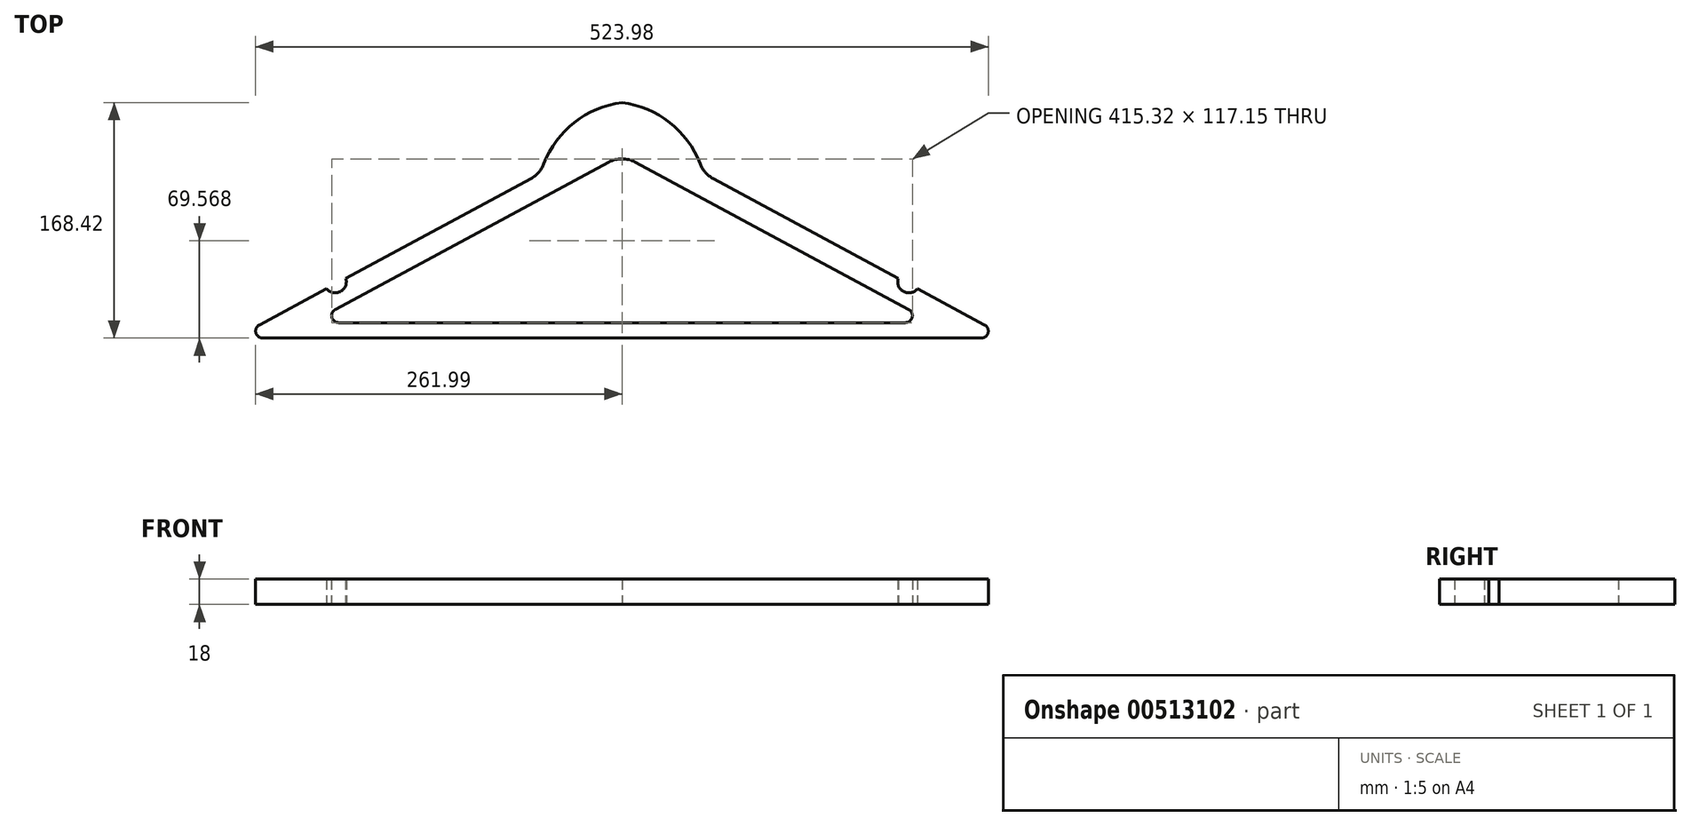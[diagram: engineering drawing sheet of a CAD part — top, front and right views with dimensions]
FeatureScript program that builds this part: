
annotation { "Feature Type Name" : "Feature", "Feature Type Description" : "" }
export const myFeature = defineFeature(function(context is Context, id is Id, definition is map)
    precondition{}
    {
        {
            var Q0;
            Q0=qCreatedBy(makeId("Top.planeOp"),FACE);
            var sketch = newSketch(context, id + "F0", { "sketchPlane" : qUnion([Q0])});
            skLineSegment(sketch, "E0", {"start": v(-230.49, 94.94) * mm, "end": v(174.87, 94.94) * mm});
            skLineSegment(sketch, "E1", {"start": v(-232.86, 104.34) * mm, "end": v(-37.3, 209.7) * mm});
            skLineSegment(sketch, "E2", {"start": v(-18.32, 209.7) * mm, "end": v(177.24, 104.34) * mm});
            skLineSegment(sketch, "E3", {"start": v(-287.17, 93.36) * mm, "end": v(-239.12, 119.24) * mm});
            skLineSegment(sketch, "E4", {"start": v(37.3, 198) * mm, "end": v(169.75, 126.65) * mm});
            skLineSegment(sketch, "E5", {"start": v(229.18, 83.95) * mm, "end": v(-284.8, 83.95) * mm});
            skLineSegment(sketch, "E6", {"start": v(-27.81, 214.81) * mm, "end": v(-27.81, -26.53) * mm, "construction": true});
            skLineSegment(sketch, "E7", {"start": v(-27.81, -26.53) * mm, "end": v(-27.81, 281.21) * mm, "construction": true});
            skPoint(sketch, "E8.visualSharp", {"position": v(-304.62, 83.95) * mm});
            skArc(sketch, "E8.filletArc", {"start": v(-287.17, 93.36) * mm, "mid": v(-289.64, 87.73) * mm, "end": v(-284.8, 83.95) * mm});
            skPoint(sketch, "E9.visualSharp", {"position": v(249, 83.95) * mm});
            skArc(sketch, "E9.filletArc", {"start": v(229.18, 83.95) * mm, "mid": v(234.02, 87.73) * mm, "end": v(231.55, 93.36) * mm});
            skPoint(sketch, "E10.visualSharp", {"position": v(-250.31, 94.94) * mm});
            skArc(sketch, "E10.filletArc", {"start": v(-232.86, 104.34) * mm, "mid": v(-235.34, 98.72) * mm, "end": v(-230.49, 94.94) * mm});
            skPoint(sketch, "E11.visualSharp", {"position": v(194.69, 94.94) * mm});
            skArc(sketch, "E11.filletArc", {"start": v(174.87, 94.94) * mm, "mid": v(179.71, 98.72) * mm, "end": v(177.24, 104.34) * mm});
            skPoint(sketch, "E12.visualSharp", {"position": v(-27.81, 256.12) * mm});
            skPoint(sketch, "E13.visualSharp", {"position": v(-27.81, 214.81) * mm});
            skArc(sketch, "E13.filletArc", {"start": v(-18.32, 209.7) * mm, "mid": v(-27.81, 212.1) * mm, "end": v(-37.3, 209.7) * mm});
            skArc(sketch, "E14", {"start": v(-27.78, 252.37) * mm, "mid": v(-61.8, 238.06) * mm, "end": v(-83.76, 208.4) * mm});
            skArc(sketch, "E15.MirrorCS", {"start": v(-27.85, 252.37) * mm, "mid": v(6.18, 238.06) * mm, "end": v(28.14, 208.4) * mm});
            skPoint(sketch, "E16.visualSharp", {"position": v(-85.95, 201.76) * mm});
            skArc(sketch, "E16.filletArc", {"start": v(-92.92, 198) * mm, "mid": v(-87.41, 202.38) * mm, "end": v(-83.76, 208.4) * mm});
            skPoint(sketch, "E17.visualSharp", {"position": v(30.33, 201.76) * mm});
            skArc(sketch, "E17.filletArc", {"start": v(28.14, 208.4) * mm, "mid": v(31.8, 202.38) * mm, "end": v(37.3, 198) * mm});
            skArc(sketch, "E18", {"start": v(-239.12, 119.24) * mm, "mid": v(-229.14, 117.17) * mm, "end": v(-225.37, 126.65) * mm});
            skLineSegment(sketch, "E19.trimOffspring", {"start": v(-225.37, 126.65) * mm, "end": v(-92.92, 198) * mm});
            skArc(sketch, "E20.MirrorCS", {"start": v(183.5, 119.24) * mm, "mid": v(173.51, 117.17) * mm, "end": v(169.75, 126.65) * mm});
            skLineSegment(sketch, "E21.trimOffspring", {"start": v(183.5, 119.24) * mm, "end": v(231.55, 93.36) * mm});
            skSolve(sketch);
        }
        {
            var Q0;
            Q0=makeQuery(id+"F0.imprint","IMPRINT",FACE,{"disambiguationData":[TD([[makeQuery(id+"F0.imprint","IMPRINT",EDGE,{"derivedFrom":sQuery(id+"F0.wireOp",EDGE,"E0")}),-1.0]])]});
            extrude(context, id + "F1", {"entities" : qUnion([Q0]), "depth" : 18 * mm});
        }
    });
